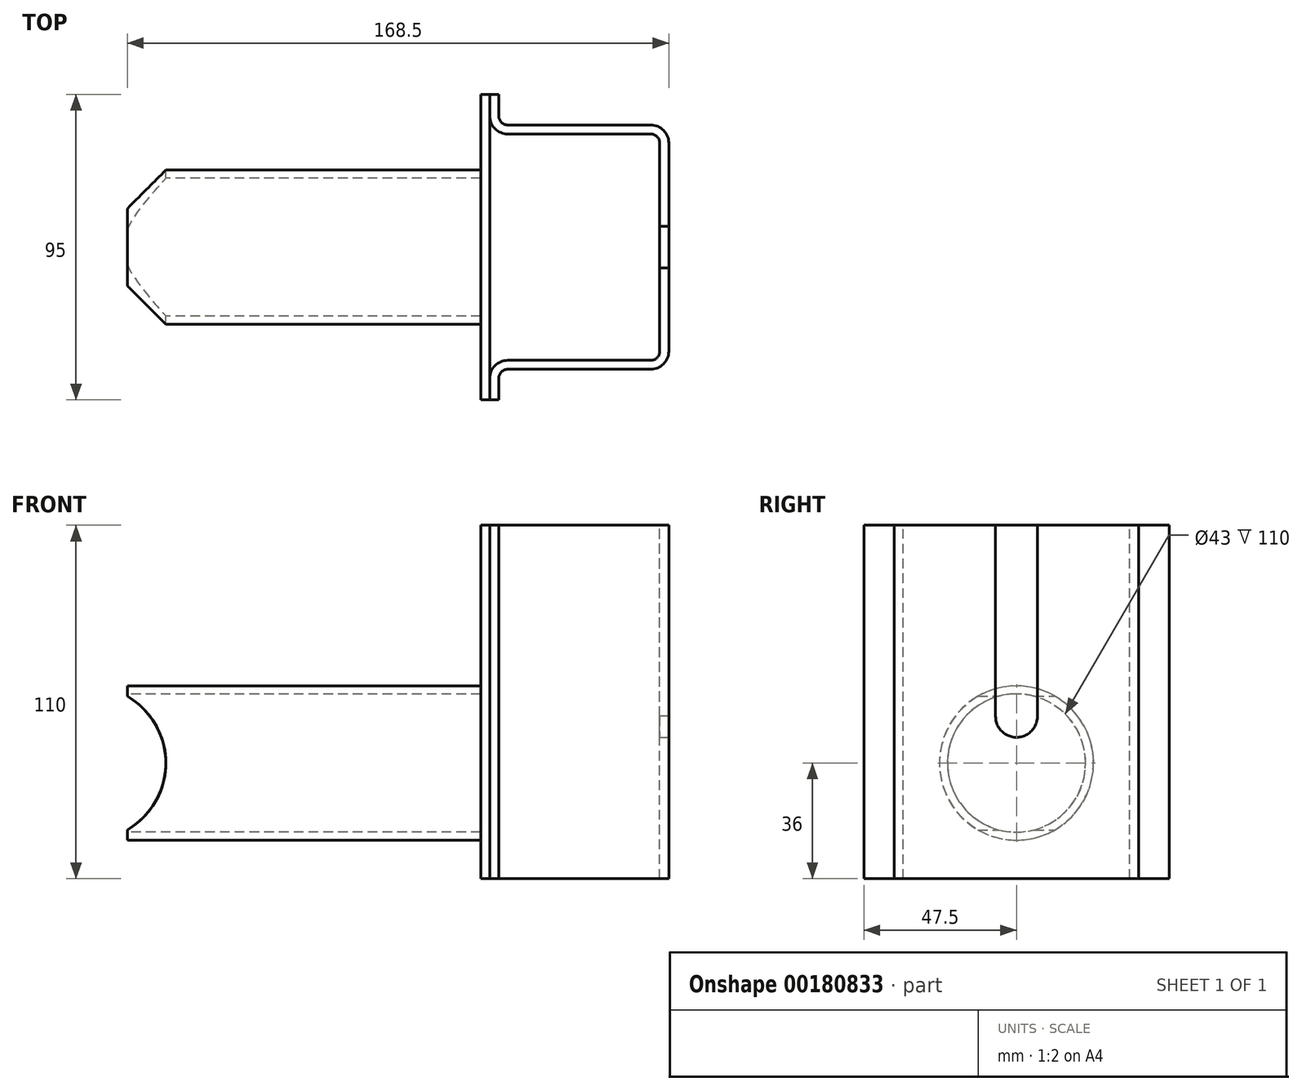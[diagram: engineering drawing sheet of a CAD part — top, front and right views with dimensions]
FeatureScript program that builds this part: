
annotation { "Feature Type Name" : "Feature", "Feature Type Description" : "" }
export const myFeature = defineFeature(function(context is Context, id is Id, definition is map)
    precondition{}
    {
        {
            var Q0;
            Q0=qCreatedBy(makeId("Front.planeOp"),FACE);
            var sketch = newSketch(context, id + "F0", { "sketchPlane" : qUnion([Q0])});
            skLineSegment(sketch, "E0", {"start": v(0, 0) * mm, "end": v(-110, 0) * mm});
            skLineSegment(sketch, "E1.0", {"start": v(0, 24) * mm, "end": v(-110, 24) * mm});
            skLineSegment(sketch, "E2", {"start": v(-110, 24) * mm, "end": v(-110, 0) * mm});
            skLineSegment(sketch, "E3", {"start": v(0, 24) * mm, "end": v(0, 0) * mm});
            skSolve(sketch);
        }
        {
            var Q0;
            Q0 = qSketchRegion(id + "F0", true);
            var Q1;
            Q1=sQuery(id+"F0.wireOp",EDGE,"E0");
            revolve(context, id + "F1", {"entities" : qUnion([Q0]), "axis" : qUnion([Q1]), "revolveType" : RevolveType.FULL});
        }
        {
            var Q0;
            Q0=qCreatedBy(makeId("Front.planeOp"),FACE);
            var sketch = newSketch(context, id + "F2", { "sketchPlane" : qUnion([Q0])});
            skCircle(sketch, "E4", {"center": v(-122, 0) * mm, "radius": 24 * mm});
            skLineSegment(sketch, "E5.0", {"start": v(-98, 24) * mm, "end": v(-98, -24) * mm});
            skSolve(sketch);
        }
        {
            var Q0;
            Q0=makeQuery(id+"F1.opRevolve","SWEPT_FACE",FACE,{"disambiguationData":[OSD([sQuery(id+"F0.wireOp",EDGE,"E2")])]});
            var sketch = newSketch(context, id + "F3", { "sketchPlane" : qUnion([Q0])});
            skSolve(sketch);
        }
        {
            var Q0;
            Q0=makeQuery(id+"F3.imprint","IMPRINT",FACE,{"disambiguationData":[TD([[makeQuery(id+"F3.imprint","IMPRINT",EDGE,{"derivedFrom":makeQuery(id+"F1.opRevolve","SWEPT_EDGE",EDGE,{"disambiguationData":[OSD([sQuery(id+"F0.wireOp",EDGE,"E1.0"),sQuery(id+"F0.wireOp",EDGE,"E2")])]})}),-1.0]])]});
            var sketch = newSketch(context, id + "F4", { "sketchPlane" : qUnion([Q0])});
            skCircle(sketch, "E6", {"center": v(0, 0) * mm, "radius": 21.5 * mm});
            skSolve(sketch);
        }
        {
            var Q0;
            Q0 = qSketchRegion(id + "F4", true);
            extrude(context, id + "F5", {"entities" : qUnion([Q0]), "operationType" : NewBodyOperationType.REMOVE, "endBound" : BoundingType.THROUGH_ALL, "oppositeDirection" : true, "depth" : 25 * mm});
        }
        {
            var Q0;
            Q0=makeQuery(id+"F2.imprint","IMPRINT",FACE,{"disambiguationData":[TD([[makeQuery(id+"F2.imprint","IMPRINT",EDGE,{"derivedFrom":sQuery(id+"F2.wireOp",EDGE,"E4")}),1.0]])]});
            extrude(context, id + "F6", {"entities" : qUnion([Q0]), "operationType" : NewBodyOperationType.REMOVE, "endBound" : BoundingType.SYMMETRIC, "depth" : 50 * mm});
        }
        {
            var Q0;
            Q0=qCreatedBy(makeId("Front.planeOp"),FACE);
            var sketch = newSketch(context, id + "F7", { "sketchPlane" : qUnion([Q0])});
            skLineSegment(sketch, "E7", {"start": v(0, 0) * mm, "end": v(0, -36) * mm});
            skLineSegment(sketch, "E8", {"start": v(0, -36) * mm, "end": v(2.8, -36) * mm});
            skLineSegment(sketch, "E9", {"start": v(2.8, -36) * mm, "end": v(2.8, 74) * mm});
            skLineSegment(sketch, "E10", {"start": v(2.8, 74) * mm, "end": v(0, 74) * mm});
            skLineSegment(sketch, "E11", {"start": v(0, 74) * mm, "end": v(0, 0) * mm});
            skSolve(sketch);
        }
        {
            var Q0;
            Q0 = qSketchRegion(id + "F7", true);
            extrude(context, id + "F8", {"entities" : qUnion([Q0]), "operationType" : NewBodyOperationType.ADD, "endBound" : BoundingType.SYMMETRIC, "depth" : 95 * mm});
        }
        {
            var Q0;
            Q0=makeQuery(id+"F8.opExtrude","SWEPT_FACE",FACE,{"disambiguationData":[OSD([sQuery(id+"F7.wireOp",EDGE,"E10")])]});
            var sketch = newSketch(context, id + "F9", { "sketchPlane" : qUnion([Q0])});
            skLineSegment(sketch, "E12.0", {"start": v(52.9, -35.2) * mm, "end": v(8.4, -35.2) * mm});
            skLineSegment(sketch, "E13.0", {"start": v(52.9, -38) * mm, "end": v(8.4, -38) * mm});
            skLineSegment(sketch, "E14.0", {"start": v(5.6, -47.5) * mm, "end": v(5.6, -40.8) * mm});
            skLineSegment(sketch, "E15", {"start": v(2.8, -40.8) * mm, "end": v(2.8, -47.5) * mm});
            skPoint(sketch, "E16.visualSharp", {"position": v(5.6, -38) * mm});
            skArc(sketch, "E16.filletArc", {"start": v(8.4, -38) * mm, "mid": v(6.42, -38.82) * mm, "end": v(5.6, -40.8) * mm});
            skPoint(sketch, "E17.visualSharp", {"position": v(55.7, -35.2) * mm});
            skArc(sketch, "E17.filletArc", {"start": v(52.9, -35.2) * mm, "mid": v(54.88, -34.38) * mm, "end": v(55.7, -32.4) * mm});
            skPoint(sketch, "E18.visualSharp", {"position": v(2.8, -35.2) * mm});
            skArc(sketch, "E18.filletArc", {"start": v(8.4, -35.2) * mm, "mid": v(4.44, -36.84) * mm, "end": v(2.8, -40.8) * mm});
            skArc(sketch, "E19.filletArc", {"start": v(52.9, -38) * mm, "mid": v(56.86, -36.36) * mm, "end": v(58.5, -32.4) * mm});
            skLineSegment(sketch, "E20.trimOffspring", {"start": v(5.6, -47.5) * mm, "end": v(2.8, -47.5) * mm});
            skLineSegment(sketch, "E21.MirrorCS", {"start": v(5.6, 47.5) * mm, "end": v(2.8, 47.5) * mm});
            skLineSegment(sketch, "E22.MirrorCS", {"start": v(2.8, 40.8) * mm, "end": v(2.8, 47.5) * mm});
            skLineSegment(sketch, "E23.MirrorCS", {"start": v(5.6, 47.5) * mm, "end": v(5.6, 40.8) * mm});
            skArc(sketch, "E24.MirrorCS", {"start": v(8.4, 35.2) * mm, "mid": v(4.44, 36.84) * mm, "end": v(2.8, 40.8) * mm});
            skArc(sketch, "E25.MirrorCS", {"start": v(8.4, 38) * mm, "mid": v(6.42, 38.82) * mm, "end": v(5.6, 40.8) * mm});
            skLineSegment(sketch, "E26.MirrorCS", {"start": v(52.9, 38) * mm, "end": v(8.4, 38) * mm});
            skLineSegment(sketch, "E27.MirrorCS", {"start": v(52.9, 35.2) * mm, "end": v(8.4, 35.2) * mm});
            skArc(sketch, "E28.MirrorCS", {"start": v(52.9, 38) * mm, "mid": v(56.86, 36.36) * mm, "end": v(58.5, 32.4) * mm});
            skArc(sketch, "E29.MirrorCS", {"start": v(52.9, 35.2) * mm, "mid": v(54.88, 34.38) * mm, "end": v(55.7, 32.4) * mm});
            skLineSegment(sketch, "E30", {"start": v(55.7, -32.4) * mm, "end": v(55.7, 32.4) * mm});
            skLineSegment(sketch, "E31", {"start": v(58.5, -32.4) * mm, "end": v(58.5, 32.4) * mm});
            skSolve(sketch);
        }
        {
            var Q0;
            Q0 = qSketchRegion(id + "F9", true);
            extrude(context, id + "F10", {"entities" : qUnion([Q0]), "oppositeDirection" : true, "depth" : 110 * mm});
        }
        {
            var Q0;
            Q0=makeQuery(id+"F10.opExtrude","SWEPT_FACE",FACE,{"disambiguationData":[OSD([sQuery(id+"F9.wireOp",EDGE,"E31")])]});
            var sketch = newSketch(context, id + "F11", { "sketchPlane" : qUnion([Q0])});
            skPoint(sketch, "E32.endSnap0", {"position": v(0, 74) * mm});
            skArc(sketch, "E33", {"start": v(-6.5, 14.5) * mm, "mid": v(0.1, 8) * mm, "end": v(6.5, 14.7) * mm});
            skLineSegment(sketch, "E34", {"start": v(-6.5, 14.5) * mm, "end": v(-6.5, 74) * mm});
            skLineSegment(sketch, "E35", {"start": v(6.5, 14.6) * mm, "end": v(6.5, 74) * mm});
            skLineSegment(sketch, "E36", {"start": v(6.5, 74) * mm, "end": v(-6.5, 74) * mm});
            skPoint(sketch, "E37.orphan", {"position": v(6.5, 14.5) * mm});
            skSolve(sketch);
        }
        {
            var Q0;
            Q0 = qSketchRegion(id + "F11", true);
            extrude(context, id + "F12", {"entities" : qUnion([Q0]), "operationType" : NewBodyOperationType.REMOVE, "oppositeDirection" : true, "depth" : 10 * mm});
        }
    });
